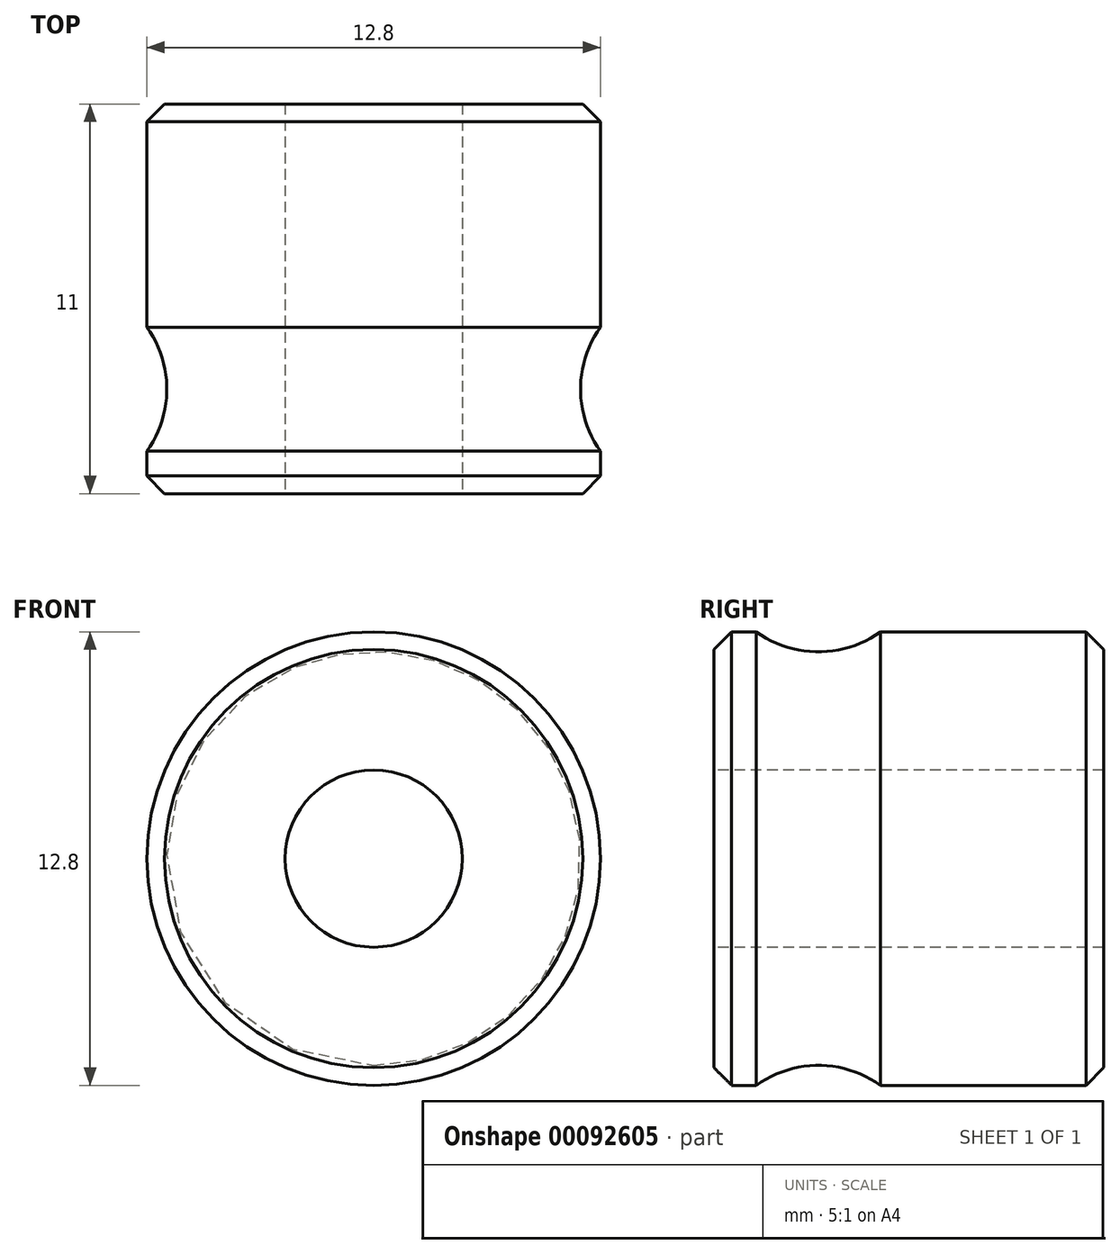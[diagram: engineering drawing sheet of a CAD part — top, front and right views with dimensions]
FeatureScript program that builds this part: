
annotation { "Feature Type Name" : "Feature", "Feature Type Description" : "" }
export const myFeature = defineFeature(function(context is Context, id is Id, definition is map)
    precondition{}
    {
        {
            var Q0;
            Q0=qCreatedBy(makeId("Right.planeOp"),FACE);
            var sketch = newSketch(context, id + "F0", { "sketchPlane" : qUnion([Q0])});
            skLineSegment(sketch, "E0", {"start": v(-5.5, 2.5) * mm, "end": v(-5.5, 6.4) * mm});
            skLineSegment(sketch, "E1", {"start": v(-5.5, 6.4) * mm, "end": v(-4.3, 6.4) * mm});
            skLineSegment(sketch, "E2", {"start": v(-0.8, 6.4) * mm, "end": v(5.5, 6.4) * mm});
            skLineSegment(sketch, "E3", {"start": v(5.5, 6.4) * mm, "end": v(5.5, 2.5) * mm});
            skLineSegment(sketch, "E4", {"start": v(5.5, 2.5) * mm, "end": v(-5.5, 2.5) * mm});
            skArc(sketch, "E5", {"start": v(-4.3, 6.4) * mm, "mid": v(-2.55, 5.84) * mm, "end": v(-0.8, 6.4) * mm});
            skSolve(sketch);
        }
        {
            var Q0;
            Q0=qCreatedBy(makeId("Right.planeOp"),FACE);
            var sketch = newSketch(context, id + "F1", { "sketchPlane" : qUnion([Q0])});
            skLineSegment(sketch, "E6", {"start": v(0, 0) * mm, "end": v(5.73, 0) * mm});
            skSolve(sketch);
        }
        {
            var Q0;
            Q0 = qSketchRegion(id + "F0", true);
            var Q1;
            Q1=sQuery(id+"F1.wireOp",EDGE,"E6");
            revolve(context, id + "F2", {"entities" : qUnion([Q0]), "axis" : qUnion([Q1]), "revolveType" : RevolveType.FULL});
        }
        {
            var Q0;
            Q0=makeQuery(id+"F2.opRevolve","SWEPT_EDGE",EDGE,{"disambiguationData":[OSD([sQuery(id+"F0.wireOp",EDGE,"E0"),sQuery(id+"F0.wireOp",EDGE,"E1")])]});
            var Q1;
            Q1=makeQuery(id+"F2.opRevolve","SWEPT_EDGE",EDGE,{"disambiguationData":[OSD([sQuery(id+"F0.wireOp",EDGE,"E2"),sQuery(id+"F0.wireOp",EDGE,"E3")])]});
            chamfer(context, id + "F3", {"entities" : qUnion([Q0, Q1]), "width" : 0.5 * mm, "tangentPropagation" : true});
        }
    });
